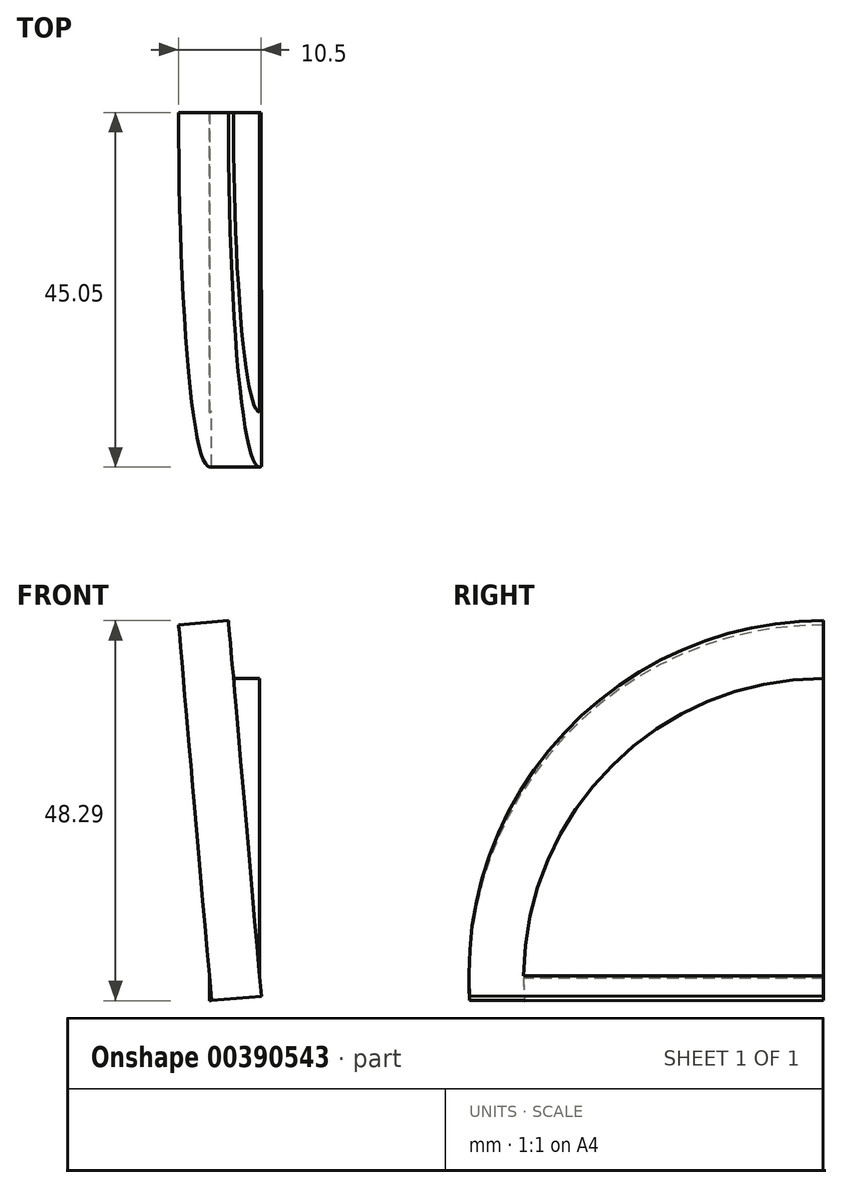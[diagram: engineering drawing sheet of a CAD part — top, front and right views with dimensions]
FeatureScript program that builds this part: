
annotation { "Feature Type Name" : "Feature", "Feature Type Description" : "" }
export const myFeature = defineFeature(function(context is Context, id is Id, definition is map)
    precondition{}
    {
        {
            var Q0;
            Q0=qCreatedBy(makeId("Right.planeOp"),FACE);
            var sketch = newSketch(context, id + "F0", { "sketchPlane" : qUnion([Q0])});
            skCircle(sketch, "E0", {"center": v(0, 0) * mm, "radius": 38.1 * mm});
            skSolve(sketch);
        }
        {
            var Q0;
            Q0=makeQuery(id+"F0.imprint","IMPRINT",FACE,{"disambiguationData":[TD([[makeQuery(id+"F0.imprint","IMPRINT",EDGE,{"derivedFrom":sQuery(id+"F0.wireOp",EDGE,"E0")}),1.0]])]});
            extrude(context, id + "F1", {"entities" : qUnion([Q0]), "depth" : 6.35 * mm});
        }
        {
            var Q0;
            Q0=qCreatedBy(makeId("Right.planeOp"),FACE);
            var sketch = newSketch(context, id + "F2", { "sketchPlane" : qUnion([Q0])});
            skLineSegment(sketch, "E1", {"start": v(0, 0) * mm, "end": v(-62.56, 0) * mm});
            skLineSegment(sketch, "E2", {"start": v(-62.56, 0) * mm, "end": v(77, 0) * mm});
            skSolve(sketch);
        }
        {
            var Q0;
            Q0=sQuery(id+"F2.wireOp",EDGE,"E2");
            cPlane(context, id + "F3", {"entities" : qUnion([Q0]), "cplaneType" : CPlaneType.LINE_ANGLE, "offset" : 25.4 * mm, "angle" : 85 * degree, "width" : 152.4 * mm, "height" : 152.4 * mm});
        }
        {
            var Q0;
            Q0=qCreatedBy(id+"F3.planeOp",FACE);
            var sketch = newSketch(context, id + "F4", { "sketchPlane" : qUnion([Q0])});
            skCircle(sketch, "E3", {"center": v(0, 0) * mm, "radius": 45.05 * mm});
            skSolve(sketch);
        }
        {
            var Q0;
            Q0=makeQuery(id+"F4.imprint","IMPRINT",FACE,{"disambiguationData":[TD([[makeQuery(id+"F4.imprint","IMPRINT",EDGE,{"derivedFrom":sQuery(id+"F4.wireOp",EDGE,"E3")}),1.0]])]});
            extrude(context, id + "F5", {"entities" : qUnion([Q0]), "operationType" : NewBodyOperationType.ADD, "depth" : 6.35 * mm});
        }
        {
            var Q0;
            Q0=makeQuery(id+"F1.opExtrude","CAP_FACE",FACE,{"disambiguationData":[OSD([sQuery(id+"F0.wireOp",EDGE,"E0")])],"isStart":true});
            var sketch = newSketch(context, id + "F6", { "sketchPlane" : qUnion([Q0])});
            skSolve(sketch);
        }
        {
            var Q0;
            Q0=makeQuery(id+"F5.opExtrude","CAP_FACE",FACE,{"disambiguationData":[OSD([sQuery(id+"F4.wireOp",EDGE,"E3")])],"isStart":false});
            cPlane(context, id + "F7", {"entities" : qUnion([Q0]), "cplaneType" : CPlaneType.OFFSET, "offset" : 25.4 * mm, "width" : 152.4 * mm, "height" : 152.4 * mm});
        }
        {
            var Q0;
            Q0=qCreatedBy(id+"F7.planeOp",FACE);
            var sketch = newSketch(context, id + "F8", { "sketchPlane" : qUnion([Q0])});
            skLineSegment(sketch, "E4", {"start": v(0, -2.77) * mm, "end": v(0, 54.2) * mm});
            skLineSegment(sketch, "E5", {"start": v(0, 54.2) * mm, "end": v(68.23, 54.2) * mm});
            skLineSegment(sketch, "E6", {"start": v(68.23, 54.2) * mm, "end": v(75.64, -57.2) * mm});
            skLineSegment(sketch, "E7", {"start": v(75.64, -57.2) * mm, "end": v(-87.02, -54.5) * mm});
            skLineSegment(sketch, "E8", {"start": v(-87.02, -54.5) * mm, "end": v(-63.26, -2.88) * mm});
            skLineSegment(sketch, "E9", {"start": v(-63.26, -2.88) * mm, "end": v(0, -2.77) * mm});
            skSolve(sketch);
        }
        {
            var Q0;
            Q0=makeQuery(id+"F8.imprint","IMPRINT",FACE,{"disambiguationData":[TD([[makeQuery(id+"F8.imprint","IMPRINT",EDGE,{"derivedFrom":sQuery(id+"F8.wireOp",EDGE,"E4")}),-1.0]])]});
            extrude(context, id + "F9", {"entities" : qUnion([Q0]), "operationType" : NewBodyOperationType.REMOVE, "oppositeDirection" : true, "depth" : 50.8 * mm});
        }
    });
